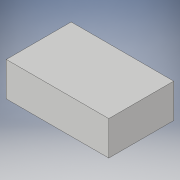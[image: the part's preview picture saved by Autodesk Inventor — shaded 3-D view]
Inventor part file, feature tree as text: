
AUTODESK INVENTOR PART (.ipt)
format: ipt  version: 2019 (Build 230136000, 136)  size: 86,528 bytes
history: native  units: mm
features: extrude x1, sketch x1
ambient origin geometry x8: Origin, YZ Plane, XZ Plane, XY Plane, X Axis, Y Axis, Z Axis, Center Point
bodies: Volumenkörper1 (feature_tree)
feature tree (2):
  extrude  "Extrusion1"  Depth=9.5mm
  sketch  "Skizze1"  dims[d0=15.0mm d1=9.5mm d2=5.0mm d3=0.0mm]
